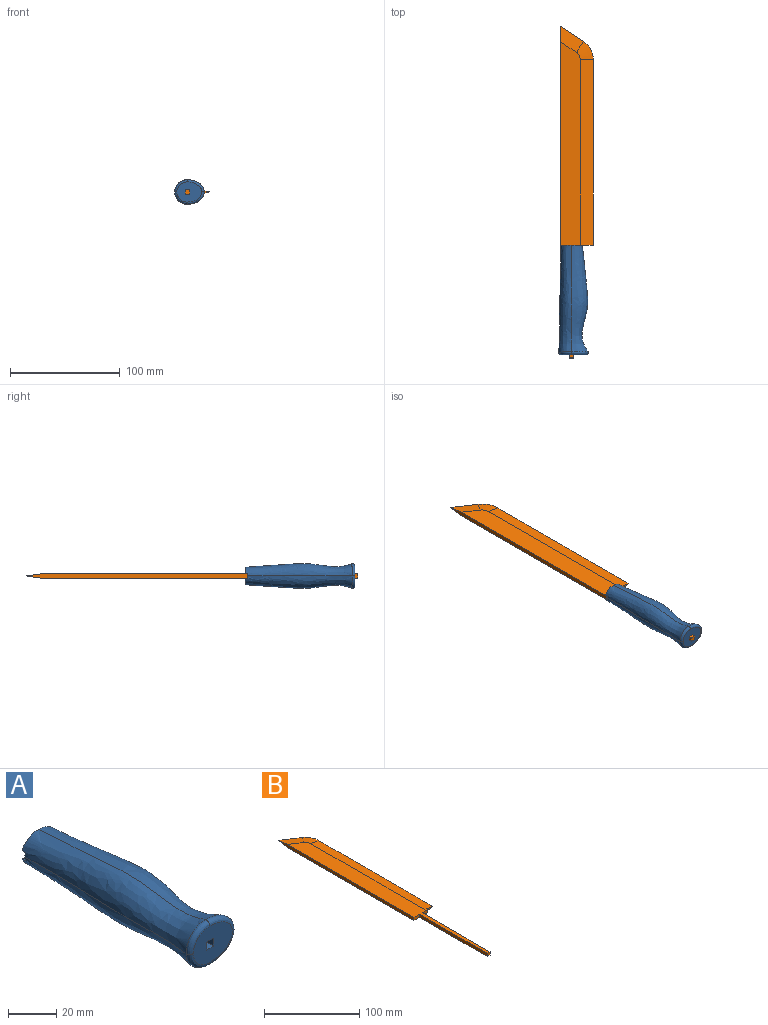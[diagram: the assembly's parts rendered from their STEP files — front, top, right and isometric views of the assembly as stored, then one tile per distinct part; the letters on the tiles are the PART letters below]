
ASSEMBLY  parts=2 mates=1
PART A: 17 faces, bbox 29.4x100x26.1 mm
  f0: plane 7.98x4.01mm, normal (0,1,0), area 31.5mm2, adj f4,f6,f8,f9,f12
  f1: plane 22.94x18.36mm, normal (0,-1,0), area 315mm2, adj f8,f9,f11,f12,f13,f14,f15,f16
  f2: plane 19.37x6mm, normal (0,1,0), area 86.1mm2, adj f6,f7,f9
  f3: bspline ~100x17.36mm, area 1703mm2, adj f4,f5,f7,f8,f10,f14
  f4: bspline ~97.78x11.75mm, area 1553.7mm2, adj f0,f3,f5,f6,f8,f16
  f5: plane 19.37x6mm, normal (0,1,0), area 86.1mm2, adj f3,f4,f8
  f6: bspline ~97.78x11.75mm, area 1553.7mm2, adj f0,f2,f4,f7,f9,f15
  f7: bspline ~100x17.37mm, area 1703mm2, adj f2,f3,f6,f9,f10,f13
  f8: plane 100x19.55mm, normal (0,0,-1), area 426.9mm2, adj f0,f1,f3,f4,f5,f10,f11,f12
  f9: plane 100x19.55mm, normal (0,0,1), area 426.9mm2, adj f0,f1,f2,f6,f7,f10,f11,f12
  f10: plane 8.23x4.01mm, normal (0,1,0), area 32.5mm2, adj f3,f7,f8,f9,f11
  f11: plane 98x4mm, normal (-1,0,0), area 392mm2, adj f1,f8,f9,f10
  f12: plane 98x4mm, normal (1,0,0), area 392mm2, adj f0,f1,f8,f9
  f13: bspline ~22.85x12.94mm, area 80.3mm2, adj f1,f7,f14,f15
  f14: bspline ~22.81x14.92mm, area 80.2mm2, adj f1,f3,f13,f16
  f15: bspline ~17.76x17.74mm, area 61.2mm2, adj f1,f6,f13,f16
  f16: bspline ~17.9x12.81mm, area 61.2mm2, adj f1,f4,f14,f15
PART B: 18 faces, bbox 30x303x4 mm
  f0: plane 10x3.33mm, normal (0,-1,0), area 16.7mm2, adj f4,f7,f16
  f1: plane 202x4mm, normal (-1,0,0), area 779.2mm2, adj f2,f3,f5,f8,f11
  f2: plane 288.58x20mm, normal (0,0,1), area 3673.6mm2, adj f1,f4,f5,f6,f11,f12,f13,f14
  f3: plane 288.58x20mm, normal (0,0,-1), area 3673.6mm2, adj f1,f7,f8,f9,f10,f11,f12,f13
  f4: plane 169.3x12mm, normal (0.16,0,0.99), area 2059.6mm2, adj f0,f2,f6,f7,f17
  f5: plane 24.05x21.09mm, normal (0.09,0.14,0.99), area 259.8mm2, adj f1,f2,f6,f8
  f6: cone r=8mm half-angle=80.5deg, axis (0,0,-1), area 167.4mm2, adj f2,f4,f5,f9
  f7: plane 169.3x12mm, normal (0.16,0,-0.99), area 2059.6mm2, adj f0,f3,f4,f9,f10
  f8: plane 24.05x21.09mm, normal (0.09,0.14,-0.99), area 259.8mm2, adj f1,f3,f5,f9
  f9: cone r=20mm half-angle=80.5deg, axis (0,0,1), area 167.4mm2, adj f3,f6,f7,f8
  f10: plane 2x0.33mm, normal (0,1,0), area 0.3mm2, adj f3,f7,f16
  f11: plane 8x4mm, normal (0,-1,0), area 32mm2, adj f1,f2,f3,f12
  f12: plane 101x4mm, normal (-1,0,0), area 404mm2, adj f2,f3,f11,f13
  f13: plane 4x4mm, normal (0,-1,0), area 16mm2, adj f2,f3,f12,f14
  f14: plane 101x4mm, normal (1,0,0), area 404mm2, adj f2,f3,f13,f15
  f15: plane 8x4mm, normal (0,-1,0), area 32mm2, adj f2,f3,f14,f16
  f16: plane 4x2mm, normal (1,0,0), area 8mm2, adj f0,f2,f3,f10,f15,f17
  f17: plane 2x0.33mm, normal (0,1,0), area 0.3mm2, adj f2,f4,f16
PLACE A at identity fixed
PLACE B t=(-0.04,0,0)mm
MATE fastened B.f15 <-> A.f10  axis (0,1,0) through (1.96,-2,2)mm
